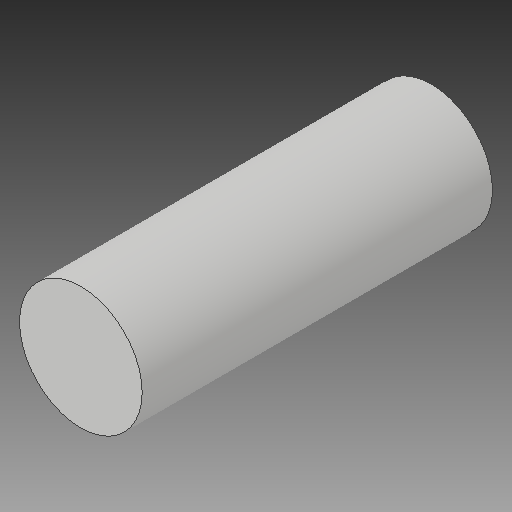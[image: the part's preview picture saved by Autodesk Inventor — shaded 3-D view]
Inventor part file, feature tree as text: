
AUTODESK INVENTOR PART (.ipt)
format: ipt  version: 2019 (Build 230136000, 136)  size: 89,600 bytes
history: native  units: mm
features: extrude x1, sketch x1
ambient origin geometry x8: Origin, YZ Plane, XZ Plane, XY Plane, X Axis, Y Axis, Z Axis, Center Point
bodies: Solid1 (feature_tree)
feature tree (2):
  extrude  "Extrusion1"  Depth=20.0mm TaperAngle=0.0deg
  sketch  "Sketch1"  dims[d0=7.0mm d1=20.0mm d2=0.0mm]
